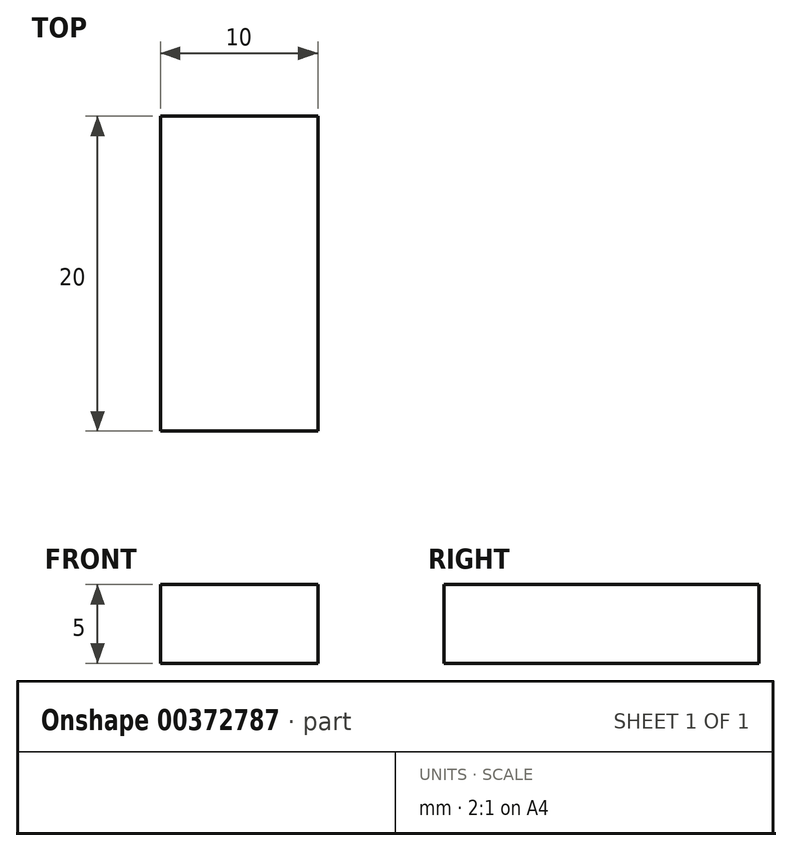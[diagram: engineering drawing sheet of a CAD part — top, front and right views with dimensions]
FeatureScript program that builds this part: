
annotation { "Feature Type Name" : "Feature", "Feature Type Description" : "" }
export const myFeature = defineFeature(function(context is Context, id is Id, definition is map)
    precondition{}
    {
        {
            var Q0;
            Q0=qCreatedBy(makeId("Front.planeOp"),FACE);
            var sketch = newSketch(context, id + "F0", { "sketchPlane" : qUnion([Q0])});
            skLineSegment(sketch, "E0.bottom", {"start": v(0, 0) * mm, "end": v(10, 0) * mm});
            skLineSegment(sketch, "E0.top", {"start": v(0, 5) * mm, "end": v(10, 5) * mm});
            skLineSegment(sketch, "E0.left", {"start": v(0, 0) * mm, "end": v(0, 5) * mm});
            skLineSegment(sketch, "E0.right", {"start": v(10, 0) * mm, "end": v(10, 5) * mm});
            skSolve(sketch);
        }
        {
            var Q0;
            Q0 = qSketchRegion(id + "F0", true);
            extrude(context, id + "F1", {"entities" : qUnion([Q0]), "depth" : 20 * mm});
        }
    });
